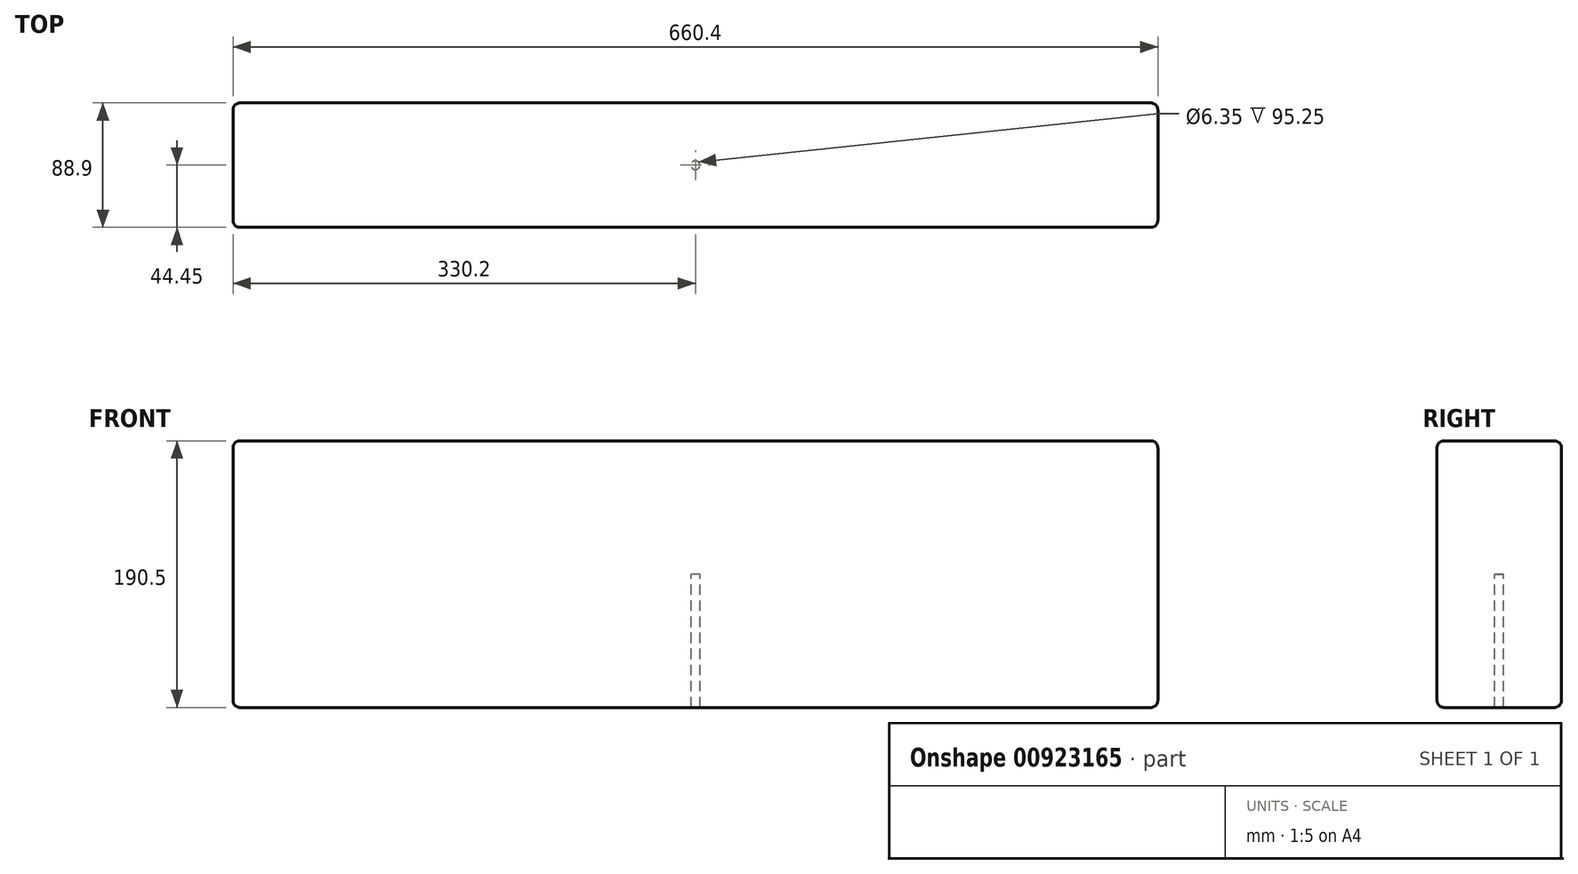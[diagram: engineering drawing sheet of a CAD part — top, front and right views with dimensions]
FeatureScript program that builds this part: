
annotation { "Feature Type Name" : "Feature", "Feature Type Description" : "" }
export const myFeature = defineFeature(function(context is Context, id is Id, definition is map)
    precondition{}
    {
        {
            var Q0;
            Q0=qCreatedBy(makeId("Right.planeOp"),FACE);
            var sketch = newSketch(context, id + "F0", { "sketchPlane" : qUnion([Q0])});
            skLineSegment(sketch, "E0.bottom", {"start": v(-44.45, 95.25) * mm, "end": v(44.45, 95.25) * mm});
            skLineSegment(sketch, "E0.top", {"start": v(-44.45, -95.25) * mm, "end": v(44.45, -95.25) * mm});
            skLineSegment(sketch, "E0.left", {"start": v(-44.45, 95.25) * mm, "end": v(-44.45, -95.25) * mm});
            skLineSegment(sketch, "E0.right", {"start": v(44.45, 95.25) * mm, "end": v(44.45, -95.25) * mm});
            skPoint(sketch, "E0.middle", {"position": v(0, 0) * mm});
            skSolve(sketch);
        }
        {
            var Q0;
            Q0=makeQuery(id+"F0.imprint","IMPRINT",FACE,{"disambiguationData":[TD([[makeQuery(id+"F0.imprint","IMPRINT",EDGE,{"derivedFrom":sQuery(id+"F0.wireOp",EDGE,"E0.bottom")}),-1.0]])]});
            extrude(context, id + "F1", {"entities" : qUnion([Q0]), "endBound" : BoundingType.SYMMETRIC, "depth" : 660.4 * mm, "offsetDistance" : 25.4 * mm});
        }
        {
            var Q0;
            Q0=qCreatedBy(makeId("Top.planeOp"),FACE);
            var sketch = newSketch(context, id + "F2", { "sketchPlane" : qUnion([Q0])});
            skCircle(sketch, "E1", {"center": v(0, 0) * mm, "radius": 3.18 * mm});
            skSolve(sketch);
        }
        {
            var Q0;
            Q0=sQuery(id+"F2.wireOp",VERTEX,"E1.center");
            var Q1;
            Q1=makeQuery(id+"F1.opExtrude","SWEPT_BODY",BODY,{"disambiguationData":[OSD([sQuery(id+"F0.wireOp",EDGE,"E0.bottom"),sQuery(id+"F0.wireOp",EDGE,"E0.top"),sQuery(id+"F0.wireOp",EDGE,"E0.left"),sQuery(id+"F0.wireOp",EDGE,"E0.right")])]});
            hole(context, id + "F3", {"style" : HoleStyle.SIMPLE, "endStyle" : HoleEndStyle.THROUGH, "holeDiameter" : 6.35 * mm, "majorDiameter" : 6.35 * mm, "isTappedThrough" : true, "tappedDepth" : 12.7 * mm, "tapClearance" : 3, "locations" : qUnion([Q0]), "scope" : qUnion([Q1])});
        }
        {
            var Q0;
            Q0=makeQuery(id+"F1.opExtrude","SWEPT_EDGE",EDGE,{"disambiguationData":[OSD([sQuery(id+"F0.wireOp",EDGE,"E0.bottom"),sQuery(id+"F0.wireOp",EDGE,"E0.left")])]});
            var Q1;
            Q1=makeQuery(id+"F1.opExtrude","SWEPT_EDGE",EDGE,{"disambiguationData":[OSD([sQuery(id+"F0.wireOp",EDGE,"E0.bottom"),sQuery(id+"F0.wireOp",EDGE,"E0.right")])]});
            var Q2;
            Q2=makeQuery(id+"F1.opExtrude","CAP_EDGE",EDGE,{"disambiguationData":[OSD([sQuery(id+"F0.wireOp",EDGE,"E0.bottom")])],"isStart":false});
            var Q3;
            Q3=makeQuery(id+"F1.opExtrude","CAP_EDGE",EDGE,{"disambiguationData":[OSD([sQuery(id+"F0.wireOp",EDGE,"E0.right")])],"isStart":false});
            var Q4;
            Q4=makeQuery(id+"F1.opExtrude","CAP_EDGE",EDGE,{"disambiguationData":[OSD([sQuery(id+"F0.wireOp",EDGE,"E0.left")])],"isStart":false});
            var Q5;
            Q5=makeQuery(id+"F1.opExtrude","CAP_EDGE",EDGE,{"disambiguationData":[OSD([sQuery(id+"F0.wireOp",EDGE,"E0.top")])],"isStart":false});
            var Q6;
            Q6=makeQuery(id+"F1.opExtrude","SWEPT_EDGE",EDGE,{"disambiguationData":[OSD([sQuery(id+"F0.wireOp",EDGE,"E0.top"),sQuery(id+"F0.wireOp",EDGE,"E0.left")])]});
            var Q7;
            Q7=makeQuery(id+"F1.opExtrude","SWEPT_EDGE",EDGE,{"disambiguationData":[OSD([sQuery(id+"F0.wireOp",EDGE,"E0.top"),sQuery(id+"F0.wireOp",EDGE,"E0.right")])]});
            var Q8;
            Q8=makeQuery(id+"F1.opExtrude","CAP_EDGE",EDGE,{"disambiguationData":[OSD([sQuery(id+"F0.wireOp",EDGE,"E0.left")])],"isStart":true});
            var Q9;
            Q9=makeQuery(id+"F1.opExtrude","CAP_EDGE",EDGE,{"disambiguationData":[OSD([sQuery(id+"F0.wireOp",EDGE,"E0.right")])],"isStart":true});
            var Q10;
            Q10=makeQuery(id+"F1.opExtrude","CAP_EDGE",EDGE,{"disambiguationData":[OSD([sQuery(id+"F0.wireOp",EDGE,"E0.bottom")])],"isStart":true});
            var Q11;
            Q11=makeQuery(id+"F1.opExtrude","CAP_EDGE",EDGE,{"disambiguationData":[OSD([sQuery(id+"F0.wireOp",EDGE,"E0.top")])],"isStart":true});
            fillet(context, id + "F4", {"entities" : qUnion([Q0, Q1, Q2, Q3, Q4, Q5, Q6, Q7, Q8, Q9, Q10, Q11]), "radius" : 5.08 * mm, "tangentPropagation" : true, "allowEdgeOverflow" : false});
        }
    });
